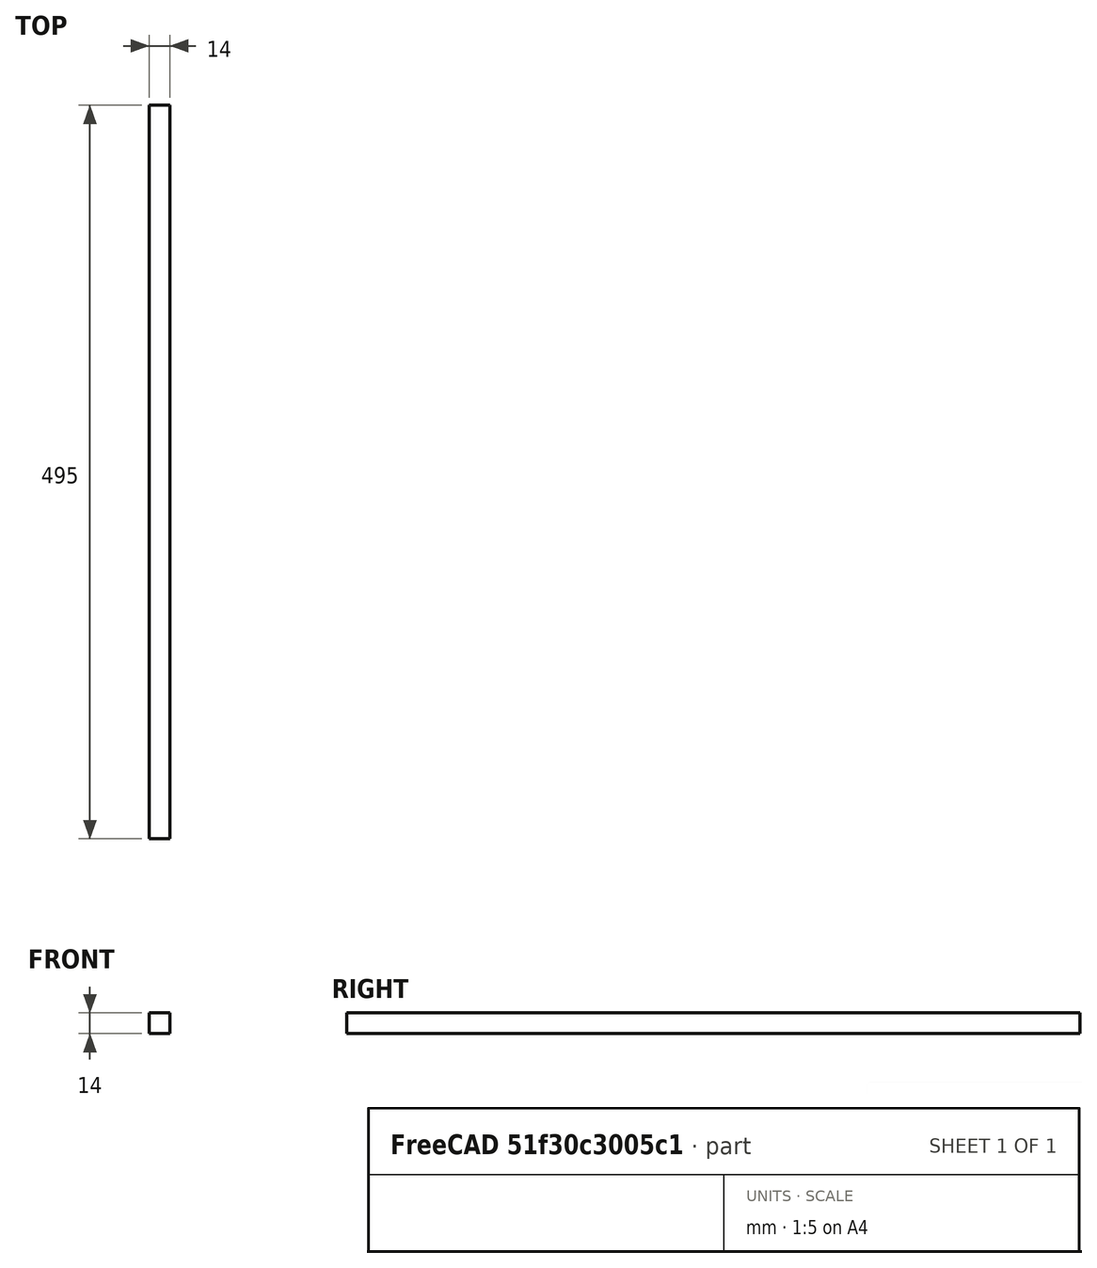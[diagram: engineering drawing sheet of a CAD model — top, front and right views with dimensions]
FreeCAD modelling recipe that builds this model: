
FCSTD DOCUMENT  (FreeCAD 0.19R24276 (Git))
Label: 3000_strut_x_14_14_495
License: All rights reserved
LicenseURL: http://en.wikipedia.org/wiki/All_rights_reserved
objects: Spreadsheet::Sheet×1, Sketcher::SketchObject×1, PartDesign::Pad×1, PartDesign::Body×1
note: 4 computed .brp shape members not serialized (recipe doc carries the construction recipe); baked Part::Feature solids carry a one-line shape summary decoded from their .brp

FEATURE [Spreadsheet::Sheet] Spreadsheet  label="xls"
  cells = B5=STRUT ; C5=14 X 14 mm; B6= width 1; C6=w1; D6(w1)=14; E6=mm; B7=Width 2; C7=w2; D7(w2)=14; E7=mm
FEATURE [Sketcher::SketchObject] Sketch
  FullyConstrained = true
  MapMode = 5
  Placement = pos=(0,0,0) rot=(1,0,0;1.5708rad)
  Support = -> [XZ_Plane]
  expr: Constraints[10] = <<xls>>.w2
  expr: Constraints[9] = <<xls>>.w1
  sketch-geometry (4):
    g0: LineSegment StartX=0 StartY=0 StartZ=0 EndX=14 EndY=0 EndZ=0
    g1: LineSegment StartX=14 StartY=0 StartZ=0 EndX=14 EndY=14 EndZ=0
    g2: LineSegment StartX=14 StartY=14 StartZ=0 EndX=0 EndY=14 EndZ=0
    g3: LineSegment StartX=0 StartY=14 StartZ=0 EndX=0 EndY=0 EndZ=0
  constraints (11):
    c: Coincident(g0,g1)
    c: Coincident(g1,g2)
    c: Coincident(g2,g3)
    c: Coincident(g3,g0)
    c: Horizontal(g0)
    c: Horizontal(g2)
    c: Vertical(g1)
    c: Vertical(g3)
    c: Coincident(g0,g-1)
    c: DistanceX(g2,g2) = 14
    c: DistanceY(g1,g1) = 14
FEATURE [PartDesign::Pad] Pad
  Direction = (1,1,1)
  Length = 495
  Length2 = 100
  Placement = pos=(0,0,0) rot=(1,0,0;1.5708rad)
  Profile = -> Sketch
  Reversed = true
  Type = 0
FEATURE [PartDesign::Body] Body
  Group = -> [Sketch,Pad]
  Origin = -> Origin
  Tip = -> Pad
